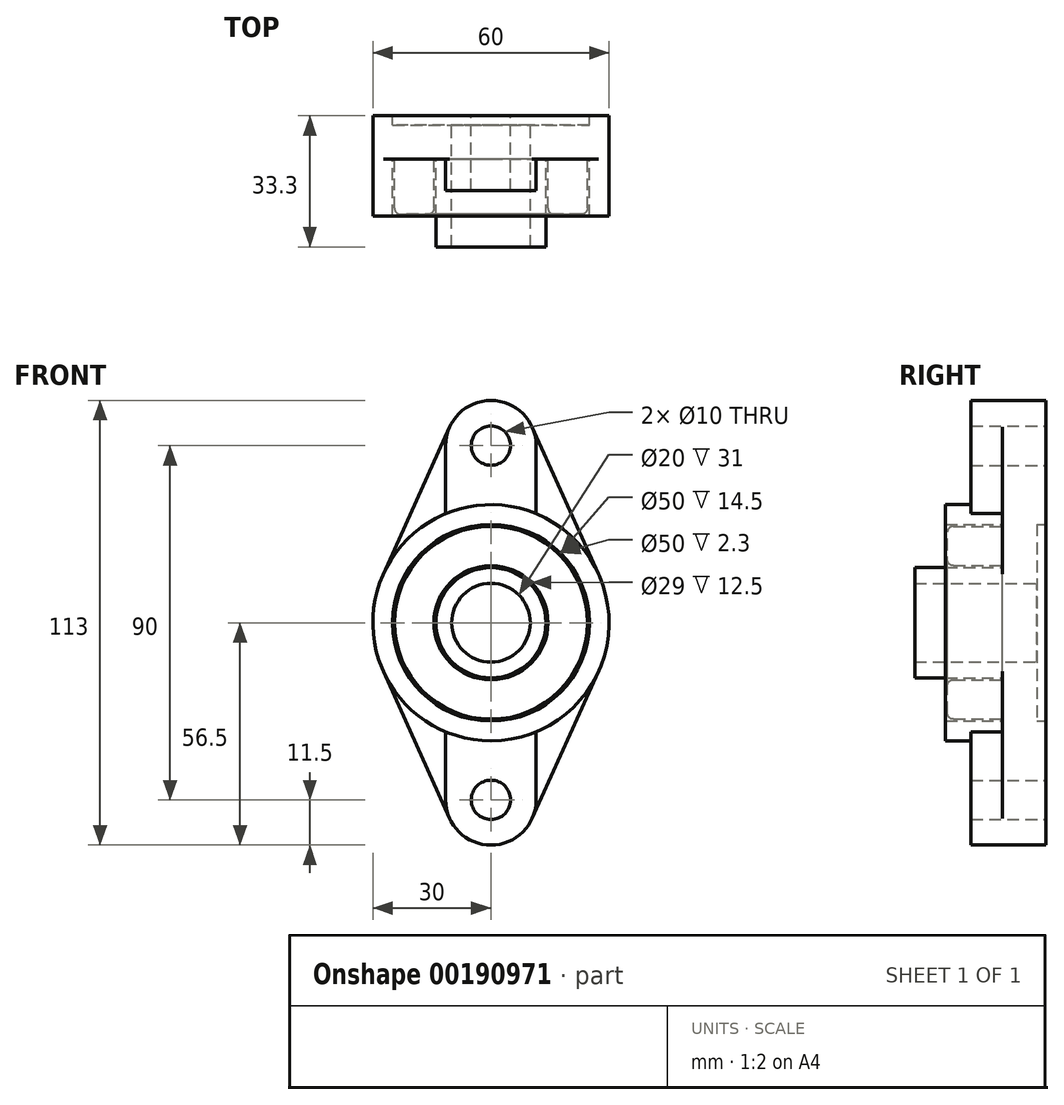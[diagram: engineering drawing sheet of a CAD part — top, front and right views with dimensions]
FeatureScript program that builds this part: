
annotation { "Feature Type Name" : "Feature", "Feature Type Description" : "" }
export const myFeature = defineFeature(function(context is Context, id is Id, definition is map)
    precondition{}
    {
        {
            var Q0;
            Q0=qCreatedBy(makeId("Front.planeOp"),FACE);
            var sketch = newSketch(context, id + "F0", { "sketchPlane" : qUnion([Q0])});
            skCircle(sketch, "E0", {"center": v(0, 0) * mm, "radius": 10 * mm});
            skCircle(sketch, "E1", {"center": v(0, 45) * mm, "radius": 5 * mm});
            skCircle(sketch, "E2", {"center": v(0, -45) * mm, "radius": 5 * mm});
            skCircle(sketch, "E3", {"center": v(0, 45) * mm, "radius": 11.5 * mm});
            skCircle(sketch, "E4", {"center": v(0, -45) * mm, "radius": 11.5 * mm});
            skCircle(sketch, "E5", {"center": v(0, 0) * mm, "radius": 30 * mm});
            skLineSegment(sketch, "E6", {"start": v(10.48, 49.73) * mm, "end": v(27.35, 12.33) * mm});
            skLineSegment(sketch, "E7.MirrorCS", {"start": v(-10.48, 49.73) * mm, "end": v(-27.35, 12.33) * mm});
            skLineSegment(sketch, "E8.MirrorCS", {"start": v(10.48, -49.73) * mm, "end": v(27.35, -12.33) * mm});
            skLineSegment(sketch, "E9.MirrorCS", {"start": v(-10.48, -49.73) * mm, "end": v(-27.35, -12.33) * mm});
            skSolve(sketch);
        }
        {
            var Q0;
            Q0 = qSketchRegion(id + "F0", true);
            extrude(context, id + "F1", {"entities" : qUnion([Q0]), "depth" : 11 * mm});
        }
        {
            var Q0;
            Q0=makeQuery(id+"F1.opExtrude","CAP_FACE",FACE,{"disambiguationData":[OSD([sQuery(id+"F0.wireOp",EDGE,"E0"),sQuery(id+"F0.wireOp",EDGE,"E1"),sQuery(id+"F0.wireOp",EDGE,"E2"),sQuery(id+"F0.wireOp",EDGE,"E3"),sQuery(id+"F0.wireOp",EDGE,"E4"),sQuery(id+"F0.wireOp",EDGE,"E5"),sQuery(id+"F0.wireOp",EDGE,"E6"),sQuery(id+"F0.wireOp",EDGE,"E7.MirrorCS"),sQuery(id+"F0.wireOp",EDGE,"E8.MirrorCS"),sQuery(id+"F0.wireOp",EDGE,"E9.MirrorCS")])],"isStart":false});
            var sketch = newSketch(context, id + "F2", { "sketchPlane" : qUnion([Q0])});
            skCircle(sketch, "E10", {"center": v(0, 0) * mm, "radius": 14 * mm});
            skCircle(sketch, "E11", {"center": v(0, 0) * mm, "radius": 10 * mm});
            skSolve(sketch);
        }
        {
            var Q0;
            Q0 = qSketchRegion(id + "F2", true);
            extrude(context, id + "F3", {"entities" : qUnion([Q0]), "operationType" : NewBodyOperationType.ADD, "depth" : 22.3 * mm});
        }
        {
            var Q0;
            Q0=makeQuery(id+"F1.opExtrude","CAP_FACE",FACE,{"disambiguationData":[OSD([sQuery(id+"F0.wireOp",EDGE,"E0"),sQuery(id+"F0.wireOp",EDGE,"E1"),sQuery(id+"F0.wireOp",EDGE,"E2"),sQuery(id+"F0.wireOp",EDGE,"E3"),sQuery(id+"F0.wireOp",EDGE,"E4"),sQuery(id+"F0.wireOp",EDGE,"E5"),sQuery(id+"F0.wireOp",EDGE,"E6"),sQuery(id+"F0.wireOp",EDGE,"E7.MirrorCS"),sQuery(id+"F0.wireOp",EDGE,"E8.MirrorCS"),sQuery(id+"F0.wireOp",EDGE,"E9.MirrorCS")])],"isStart":false});
            var sketch = newSketch(context, id + "F4", { "sketchPlane" : qUnion([Q0])});
            skCircle(sketch, "E12", {"center": v(0, 0) * mm, "radius": 30 * mm});
            skCircle(sketch, "E13", {"center": v(0, 0) * mm, "radius": 25 * mm});
            skSolve(sketch);
        }
        {
            var Q0;
            Q0 = qSketchRegion(id + "F4", true);
            extrude(context, id + "F5", {"entities" : qUnion([Q0]), "operationType" : NewBodyOperationType.ADD, "depth" : 14.5 * mm});
        }
        {
            var Q0;
            {var subQ0=sQuery(id+"F0.wireOp",EDGE,"E7.MirrorCS");var subQ1=sQuery(id+"F0.wireOp",EDGE,"E5");var subQ2=sQuery(id+"F0.wireOp",EDGE,"E9.MirrorCS");var subQ3=sQuery(id+"F0.wireOp",EDGE,"E3");var subQ4=sQuery(id+"F0.wireOp",EDGE,"E6");var subQ5=sQuery(id+"F0.wireOp",EDGE,"E8.MirrorCS");var subQ6=sQuery(id+"F0.wireOp",EDGE,"E1");Q0=makeQuery(id+"F5.boolean.opBoolean","SPLIT",FACE,{"disambiguationData":[TD([makeQuery(id+"F1.opExtrude","SWEPT_FACE",FACE,{"disambiguationData":[OSD([subQ6])]})])],"derivedFrom":makeQuery(id+"F1.opExtrude","CAP_FACE",FACE,{"disambiguationData":[OSD([sQuery(id+"F0.wireOp",EDGE,"E0"),subQ6,sQuery(id+"F0.wireOp",EDGE,"E2"),subQ3,sQuery(id+"F0.wireOp",EDGE,"E4"),subQ1,subQ4,subQ0,subQ5,subQ2])],"isStart":false})});}
            var sketch = newSketch(context, id + "F6", { "sketchPlane" : qUnion([Q0])});
            skCircle(sketch, "E14", {"center": v(0, 45) * mm, "radius": 5 * mm});
            skCircle(sketch, "E15", {"center": v(0, 45) * mm, "radius": 11.5 * mm});
            skCircle(sketch, "E16", {"center": v(0, 0) * mm, "radius": 30 * mm});
            skCircle(sketch, "E17", {"center": v(0, -45) * mm, "radius": 5 * mm});
            skCircle(sketch, "E18", {"center": v(0, -45) * mm, "radius": 11.5 * mm});
            skLineSegment(sketch, "E19", {"start": v(-11.5, 45) * mm, "end": v(-11.5, 27.7) * mm});
            skLineSegment(sketch, "E20", {"start": v(11.5, 45) * mm, "end": v(11.5, 27.7) * mm});
            skLineSegment(sketch, "E21", {"start": v(-11.5, -27.7) * mm, "end": v(-11.5, -45) * mm});
            skLineSegment(sketch, "E22", {"start": v(11.5, -27.7) * mm, "end": v(11.5, -45) * mm});
            skSolve(sketch);
        }
        {
            var Q0;
            Q0=makeQuery(id+"F6.imprint","IMPRINT",FACE,{"disambiguationData":[TD([[makeQuery(id+"F6.imprint","IMPRINT",EDGE,{"derivedFrom":sQuery(id+"F6.wireOp",EDGE,"E14")}),-1.0]])]});
            var Q1;
            {var subQ0=sQuery(id+"F6.wireOp",EDGE,"E19");Q1=makeQuery(id+"F6.imprint","IMPRINT",FACE,{"disambiguationData":[TD([[makeQuery(id+"F6.imprint","IMPRINT",EDGE,{"derivedFrom":subQ0}),1.0]])]});}
            var Q2;
            {var subQ0=sQuery(id+"F6.wireOp",EDGE,"E21");Q2=makeQuery(id+"F6.imprint","IMPRINT",FACE,{"disambiguationData":[TD([[makeQuery(id+"F6.imprint","IMPRINT",EDGE,{"derivedFrom":subQ0}),1.0]])]});}
            var Q3;
            Q3=makeQuery(id+"F6.imprint","IMPRINT",FACE,{"disambiguationData":[TD([[makeQuery(id+"F6.imprint","IMPRINT",EDGE,{"derivedFrom":sQuery(id+"F6.wireOp",EDGE,"E17")}),-1.0]])]});
            extrude(context, id + "F7", {"entities" : qUnion([Q0, Q1, Q2, Q3]), "operationType" : NewBodyOperationType.ADD, "depth" : 8 * mm});
        }
        {
            var Q0;
            Q0=makeQuery(id+"F1.opExtrude","CAP_FACE",FACE,{"disambiguationData":[OSD([sQuery(id+"F0.wireOp",EDGE,"E0"),sQuery(id+"F0.wireOp",EDGE,"E1"),sQuery(id+"F0.wireOp",EDGE,"E2"),sQuery(id+"F0.wireOp",EDGE,"E3"),sQuery(id+"F0.wireOp",EDGE,"E4"),sQuery(id+"F0.wireOp",EDGE,"E5"),sQuery(id+"F0.wireOp",EDGE,"E6"),sQuery(id+"F0.wireOp",EDGE,"E7.MirrorCS"),sQuery(id+"F0.wireOp",EDGE,"E8.MirrorCS"),sQuery(id+"F0.wireOp",EDGE,"E9.MirrorCS")])],"isStart":true});
            var sketch = newSketch(context, id + "F8", { "sketchPlane" : qUnion([Q0])});
            skCircle(sketch, "E23", {"center": v(0, 0) * mm, "radius": 25 * mm});
            skCircle(sketch, "E24", {"center": v(0, 0) * mm, "radius": 10 * mm});
            skSolve(sketch);
        }
        {
            var Q0;
            Q0=makeQuery(id+"F8.imprint","IMPRINT",FACE,{"disambiguationData":[TD([[makeQuery(id+"F8.imprint","IMPRINT",EDGE,{"derivedFrom":sQuery(id+"F8.wireOp",EDGE,"E23")}),1.0]])]});
            extrude(context, id + "F9", {"entities" : qUnion([Q0]), "operationType" : NewBodyOperationType.REMOVE, "oppositeDirection" : true, "depth" : 2.3 * mm});
        }
        {
            var Q0;
            Q0=makeQuery(id+"F5.boolean.opBoolean","SPLIT",FACE,{"disambiguationData":[TD([makeQuery(id+"F3.opExtrude","SWEPT_FACE",FACE,{"disambiguationData":[OSD([sQuery(id+"F2.wireOp",EDGE,"E10")])]})])],"derivedFrom":makeQuery(id+"F1.opExtrude","CAP_FACE",FACE,{"disambiguationData":[OSD([sQuery(id+"F0.wireOp",EDGE,"E0"),sQuery(id+"F0.wireOp",EDGE,"E1"),sQuery(id+"F0.wireOp",EDGE,"E2"),sQuery(id+"F0.wireOp",EDGE,"E3"),sQuery(id+"F0.wireOp",EDGE,"E4"),sQuery(id+"F0.wireOp",EDGE,"E5"),sQuery(id+"F0.wireOp",EDGE,"E6"),sQuery(id+"F0.wireOp",EDGE,"E7.MirrorCS"),sQuery(id+"F0.wireOp",EDGE,"E8.MirrorCS"),sQuery(id+"F0.wireOp",EDGE,"E9.MirrorCS")])],"isStart":false})});
            var sketch = newSketch(context, id + "F10", { "sketchPlane" : qUnion([Q0])});
            skCircle(sketch, "E25", {"center": v(0, 0) * mm, "radius": 14.5 * mm});
            skCircle(sketch, "E26", {"center": v(0, 0) * mm, "radius": 24.5 * mm});
            skSolve(sketch);
        }
        {
            var Q0;
            Q0=makeQuery(id+"F10.imprint","IMPRINT",FACE,{"disambiguationData":[TD([[makeQuery(id+"F10.imprint","IMPRINT",EDGE,{"derivedFrom":sQuery(id+"F10.wireOp",EDGE,"E25")}),-1.0]])]});
            extrude(context, id + "F11", {"entities" : qUnion([Q0]), "operationType" : NewBodyOperationType.ADD, "depth" : 14 * mm});
        }
        {
            var Q0;
            Q0=makeQuery(id+"F11.opExtrude","CAP_EDGE",EDGE,{"disambiguationData":[OSD([sQuery(id+"F10.wireOp",EDGE,"E26")])],"isStart":false});
            var Q1;
            Q1=makeQuery(id+"F11.opExtrude","CAP_EDGE",EDGE,{"disambiguationData":[OSD([sQuery(id+"F10.wireOp",EDGE,"E25")])],"isStart":false});
            fillet(context, id + "F12", {"entities" : qUnion([Q0, Q1]), "radius" : 1.5 * mm, "tangentPropagation" : true, "allowEdgeOverflow" : false});
        }
    });
